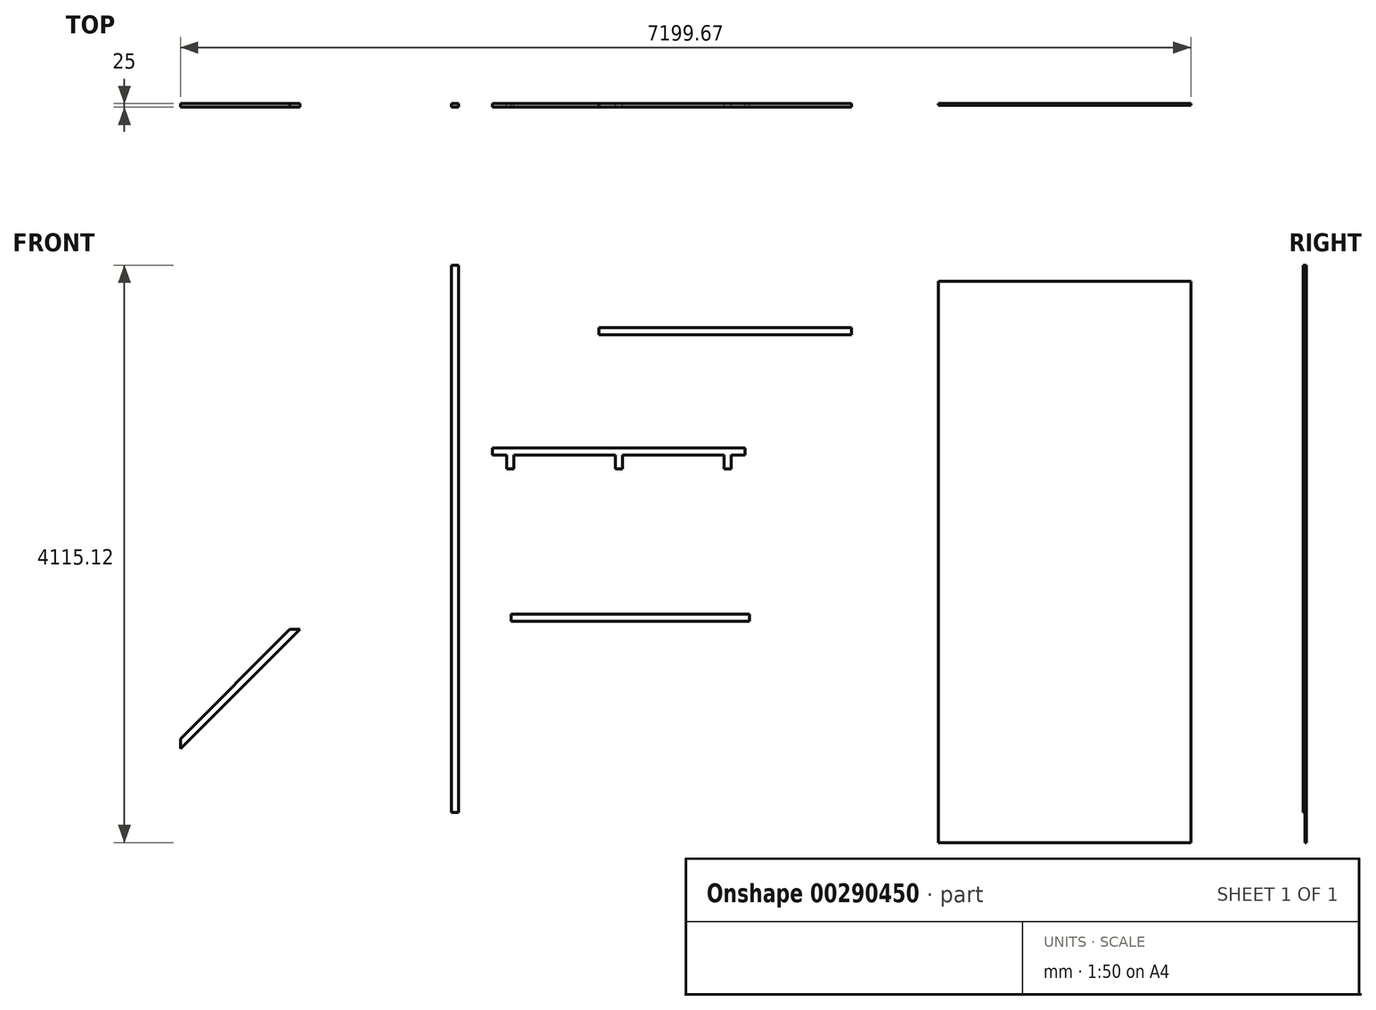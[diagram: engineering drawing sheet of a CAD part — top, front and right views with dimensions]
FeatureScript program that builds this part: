
annotation { "Feature Type Name" : "Feature", "Feature Type Description" : "" }
export const myFeature = defineFeature(function(context is Context, id is Id, definition is map)
    precondition{}
    {
        {
            var Q0;
            Q0=qCreatedBy(makeId("Front.planeOp"),FACE);
            var sketch = newSketch(context, id + "F0", { "sketchPlane" : qUnion([Q0])});
            skLineSegment(sketch, "E0.bottom", {"start": v(-102.44, 3828.48) * mm, "end": v(-52.44, 3828.48) * mm});
            skLineSegment(sketch, "E0.top", {"start": v(-102.44, -71.52) * mm, "end": v(-52.44, -71.52) * mm});
            skLineSegment(sketch, "E0.left", {"start": v(-102.44, 3828.48) * mm, "end": v(-102.44, -71.52) * mm});
            skLineSegment(sketch, "E0.right", {"start": v(-52.44, 3828.48) * mm, "end": v(-52.44, -71.52) * mm});
            skSolve(sketch);
        }
        {
            var Q0;
            Q0 = qSketchRegion(id + "F0", true);
            extrude(context, id + "F1", {"entities" : qUnion([Q0]), "depth" : 25 * mm});
        }
        {
            var Q0;
            Q0=qCreatedBy(makeId("Front.planeOp"),FACE);
            var sketch = newSketch(context, id + "F2", { "sketchPlane" : qUnion([Q0])});
            skLineSegment(sketch, "E1.bottom", {"start": v(947.7, 3383.3) * mm, "end": v(2747.7, 3383.3) * mm});
            skLineSegment(sketch, "E1.top", {"start": v(947.7, 3333.3) * mm, "end": v(2747.7, 3333.3) * mm});
            skLineSegment(sketch, "E1.left", {"start": v(947.7, 3383.3) * mm, "end": v(947.7, 3333.3) * mm});
            skLineSegment(sketch, "E1.right", {"start": v(2747.7, 3383.3) * mm, "end": v(2747.7, 3333.3) * mm});
            skSolve(sketch);
        }
        {
            var Q0;
            Q0 = qSketchRegion(id + "F2", true);
            extrude(context, id + "F3", {"entities" : qUnion([Q0]), "depth" : 25 * mm});
        }
        {
            var Q0;
            Q0=qCreatedBy(makeId("Front.planeOp"),FACE);
            var sketch = newSketch(context, id + "F4", { "sketchPlane" : qUnion([Q0])});
            skLineSegment(sketch, "E2.bottom", {"start": v(189.14, 2525.72) * mm, "end": v(1989.14, 2525.72) * mm});
            skLineSegment(sketch, "E2.left", {"start": v(189.14, 2525.72) * mm, "end": v(189.14, 2475.72) * mm});
            skLineSegment(sketch, "E2.right", {"start": v(1989.14, 2525.72) * mm, "end": v(1989.14, 2475.72) * mm});
            skLineSegment(sketch, "E3", {"start": v(289.14, 2475.72) * mm, "end": v(289.14, 2375.72) * mm});
            skLineSegment(sketch, "E4", {"start": v(289.14, 2375.72) * mm, "end": v(339.14, 2375.72) * mm});
            skLineSegment(sketch, "E5", {"start": v(339.14, 2375.72) * mm, "end": v(339.14, 2475.72) * mm});
            skLineSegment(sketch, "E6", {"start": v(1064.14, 2475.72) * mm, "end": v(1064.14, 2375.72) * mm});
            skLineSegment(sketch, "E7", {"start": v(1064.14, 2375.72) * mm, "end": v(1114.14, 2375.72) * mm});
            skLineSegment(sketch, "E8", {"start": v(1114.14, 2375.72) * mm, "end": v(1114.14, 2475.72) * mm});
            skLineSegment(sketch, "E9", {"start": v(1114.14, 2475.72) * mm, "end": v(1839.14, 2475.72) * mm});
            skLineSegment(sketch, "E10", {"start": v(1839.14, 2475.72) * mm, "end": v(1839.14, 2375.72) * mm});
            skLineSegment(sketch, "E11", {"start": v(1839.14, 2375.72) * mm, "end": v(1889.14, 2375.72) * mm});
            skLineSegment(sketch, "E12", {"start": v(1889.14, 2375.72) * mm, "end": v(1889.14, 2475.72) * mm});
            skLineSegment(sketch, "E13", {"start": v(1889.14, 2475.72) * mm, "end": v(1989.14, 2475.72) * mm});
            skLineSegment(sketch, "E14", {"start": v(189.14, 2475.72) * mm, "end": v(289.14, 2475.72) * mm});
            skLineSegment(sketch, "E15", {"start": v(339.14, 2475.72) * mm, "end": v(1064.14, 2475.72) * mm});
            skSolve(sketch);
        }
        {
            var Q0;
            Q0=makeQuery(id+"F4.imprint","IMPRINT",FACE,{"disambiguationData":[TD([[makeQuery(id+"F4.imprint","IMPRINT",EDGE,{"derivedFrom":sQuery(id+"F4.wireOp",EDGE,"E2.bottom")}),-1.0]])]});
            extrude(context, id + "F5", {"entities" : qUnion([Q0]), "depth" : 25 * mm});
        }
        {
            var Q0;
            Q0=qCreatedBy(makeId("Front.planeOp"),FACE);
            var sketch = newSketch(context, id + "F6", { "sketchPlane" : qUnion([Q0])});
            skLineSegment(sketch, "E16.left", {"start": v(320.94, 1340.2) * mm, "end": v(320.94, 1290.2) * mm});
            skLineSegment(sketch, "E17", {"start": v(320.94, 1340.2) * mm, "end": v(2020.94, 1340.2) * mm});
            skLineSegment(sketch, "E18", {"start": v(2020.94, 1340.2) * mm, "end": v(2020.94, 1290.2) * mm});
            skLineSegment(sketch, "E19", {"start": v(2020.94, 1290.2) * mm, "end": v(320.94, 1290.2) * mm});
            skSolve(sketch);
        }
        {
            var Q0;
            Q0 = qSketchRegion(id + "F6", true);
            extrude(context, id + "F7", {"entities" : qUnion([Q0]), "depth" : 25 * mm});
        }
        {
            var Q0;
            Q0=qCreatedBy(makeId("Front.planeOp"),FACE);
            var sketch = newSketch(context, id + "F8", { "sketchPlane" : qUnion([Q0])});
            skLineSegment(sketch, "E20.bottom", {"start": v(3365, 3713.36) * mm, "end": v(5165, 3713.36) * mm});
            skLineSegment(sketch, "E20.top", {"start": v(3365, -286.64) * mm, "end": v(5165, -286.64) * mm});
            skLineSegment(sketch, "E20.left", {"start": v(3365, 3713.36) * mm, "end": v(3365, -286.64) * mm});
            skLineSegment(sketch, "E20.right", {"start": v(5165, 3713.36) * mm, "end": v(5165, -286.64) * mm});
            skSolve(sketch);
        }
        {
            var Q0;
            Q0=makeQuery(id+"F8.imprint","IMPRINT",FACE,{"disambiguationData":[TD([[makeQuery(id+"F8.imprint","IMPRINT",EDGE,{"derivedFrom":sQuery(id+"F8.wireOp",EDGE,"E20.bottom")}),-1.0]])]});
            extrude(context, id + "F9", {"entities" : qUnion([Q0]), "depth" : 10 * mm});
        }
        {
            var Q0;
            Q0=qCreatedBy(makeId("Front.planeOp"),FACE);
            var sketch = newSketch(context, id + "F10", { "sketchPlane" : qUnion([Q0])});
            skLineSegment(sketch, "E21", {"start": v(-1184.66, 1231.96) * mm, "end": v(-2034.66, 381.96) * mm});
            skLineSegment(sketch, "E22", {"start": v(-2034.66, 381.96) * mm, "end": v(-2034.66, 452.67) * mm});
            skLineSegment(sketch, "E23", {"start": v(-1184.66, 1231.96) * mm, "end": v(-1255.37, 1231.96) * mm});
            skLineSegment(sketch, "E24", {"start": v(-1255.37, 1231.96) * mm, "end": v(-1184.66, 1231.96) * mm});
            skLineSegment(sketch, "E25", {"start": v(-1255.37, 1231.96) * mm, "end": v(-2034.66, 452.67) * mm});
            skSolve(sketch);
        }
        {
            var Q0;
            Q0=makeQuery(id+"F10.imprint","IMPRINT",FACE,{"disambiguationData":[TD([[makeQuery(id+"F10.imprint","IMPRINT",EDGE,{"derivedFrom":sQuery(id+"F10.wireOp",EDGE,"E21")}),-1.0]])]});
            extrude(context, id + "F11", {"entities" : qUnion([Q0]), "depth" : 25 * mm});
        }
    });
